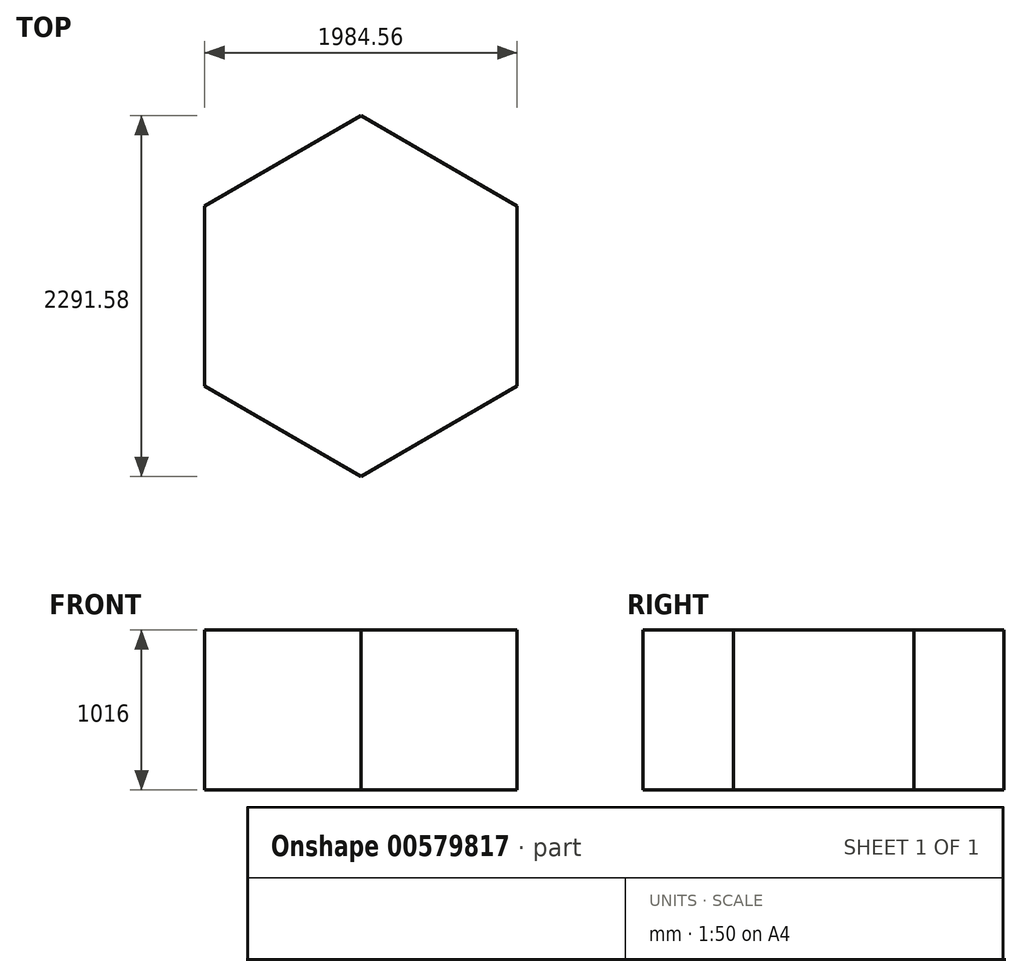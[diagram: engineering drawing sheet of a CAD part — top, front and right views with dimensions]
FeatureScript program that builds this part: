
annotation { "Feature Type Name" : "Feature", "Feature Type Description" : "" }
export const myFeature = defineFeature(function(context is Context, id is Id, definition is map)
    precondition{}
    {
        {
            var Q0;
            Q0=qCreatedBy(makeId("Top.planeOp"),FACE);
            var sketch = newSketch(context, id + "F0", { "sketchPlane" : qUnion([Q0])});
            skCircle(sketch, "E0.cCircle", {"center": v(0, 0) * mm, "radius": 992.28 * mm, "construction": true});
            skLineSegment(sketch, "E0.0", {"start": v(992.28, 572.9) * mm, "end": v(992.28, -572.9) * mm});
            skLineSegment(sketch, "E0.1", {"start": v(992.28, -572.9) * mm, "end": v(0, -1145.8) * mm});
            skLineSegment(sketch, "E0.2", {"start": v(0, -1145.8) * mm, "end": v(-992.28, -572.9) * mm});
            skLineSegment(sketch, "E0.3", {"start": v(-992.28, -572.9) * mm, "end": v(-992.28, 572.9) * mm});
            skLineSegment(sketch, "E0.4", {"start": v(-992.28, 572.9) * mm, "end": v(0, 1145.8) * mm});
            skLineSegment(sketch, "E0.5", {"start": v(0, 1145.8) * mm, "end": v(992.28, 572.9) * mm});
            skPoint(sketch, "E0.0.midPoint", {"position": v(992.28, 0) * mm});
            skSolve(sketch);
        }
        {
            var Q0;
            Q0 = qSketchRegion(id + "F0", true);
            extrude(context, id + "F1", {"entities" : qUnion([Q0]), "depth" : 1016 * mm, "offsetDistance" : 25.4 * mm});
        }
    });
